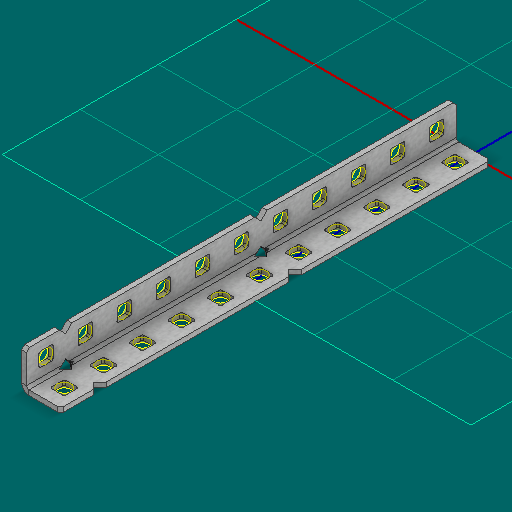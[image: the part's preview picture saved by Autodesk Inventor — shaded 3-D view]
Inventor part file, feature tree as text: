
AUTODESK INVENTOR PART (.ipt)
format: ipt  version: 2025 (Build 290162000, 162)  size: 609,280 bytes
history: native  units: in
note: dims shown in document units (in); Inventor stores cm internally (conversion verified against a paired STEP export)
features: other x53, sketch x2, sheet_metal_op x1
ambient origin geometry x8: Origin, YZ Plane, XZ Plane, XY Plane, X Axis, Y Axis, Z Axis, Center Point
bodies: Solid1 (feature_tree)
feature tree (56):
  other  "Alu Angle 1x1x11.ipt"
  other  "Solid1::Alu Angle 1x1x11.ipt"
  other  "TaggingFeature1"
  sketch  "Sketch1"  dims[d0=0.3937in]
  sketch  "Sketch2"  dims[d1=0.0625in]
  sheet_metal_op  "Body Pattern Sketch"
  other  "Arc Length"
  other  "Diagonal Plane"
  other  "Srf1"
  other  "Srf2"
  other  "Srf3"
  other  "Srf4"
  other  "Srf5"
  other  "Srf6"
  other  "Srf7"
  other  "Srf8"
  other  "Srf9"
  other  "Srf10"
  other  "Srf11"
  other  "Srf12"
  other  "Srf13"
  other  "Srf14"
  other  "Srf15"
  other  "Srf16"
  other  "Srf17"
  other  "Srf18"
  other  "Srf19"
  other  "Srf20"
  other  "Srf21"
  other  "Srf22"
  other  "Srf23"
  other  "Srf24"
  other  "Srf91::Derived"
  other  "Srf92::Derived"
  other  "Srf856::Derived"
  other  "Srf857::Derived"
  other  "Srf858::Derived"
  other  "Srf859::Derived"
  other  "Srf860::Derived"
  other  "Srf861::Derived"
  other  "Srf1383::Derived"
  other  "Srf1384::Derived"
  other  "Srf1385::Derived"
  other  "Srf1386::Derived"
  other  "Srf1275::Derived"
  other  "Srf1276::Derived"
  other  "Srf1278::Derived"
  other  "Srf1279::Derived"
  other  "Srf1280::Derived"
  other  "Srf1281::Derived"
  other  "Srf1282::Derived"
  other  "Srf1283::Derived"
  other  "Srf1475::Derived"
  other  "Srf1476::Derived"
  other  "Srf1477::Derived"
  other  "Srf1478::Derived"
